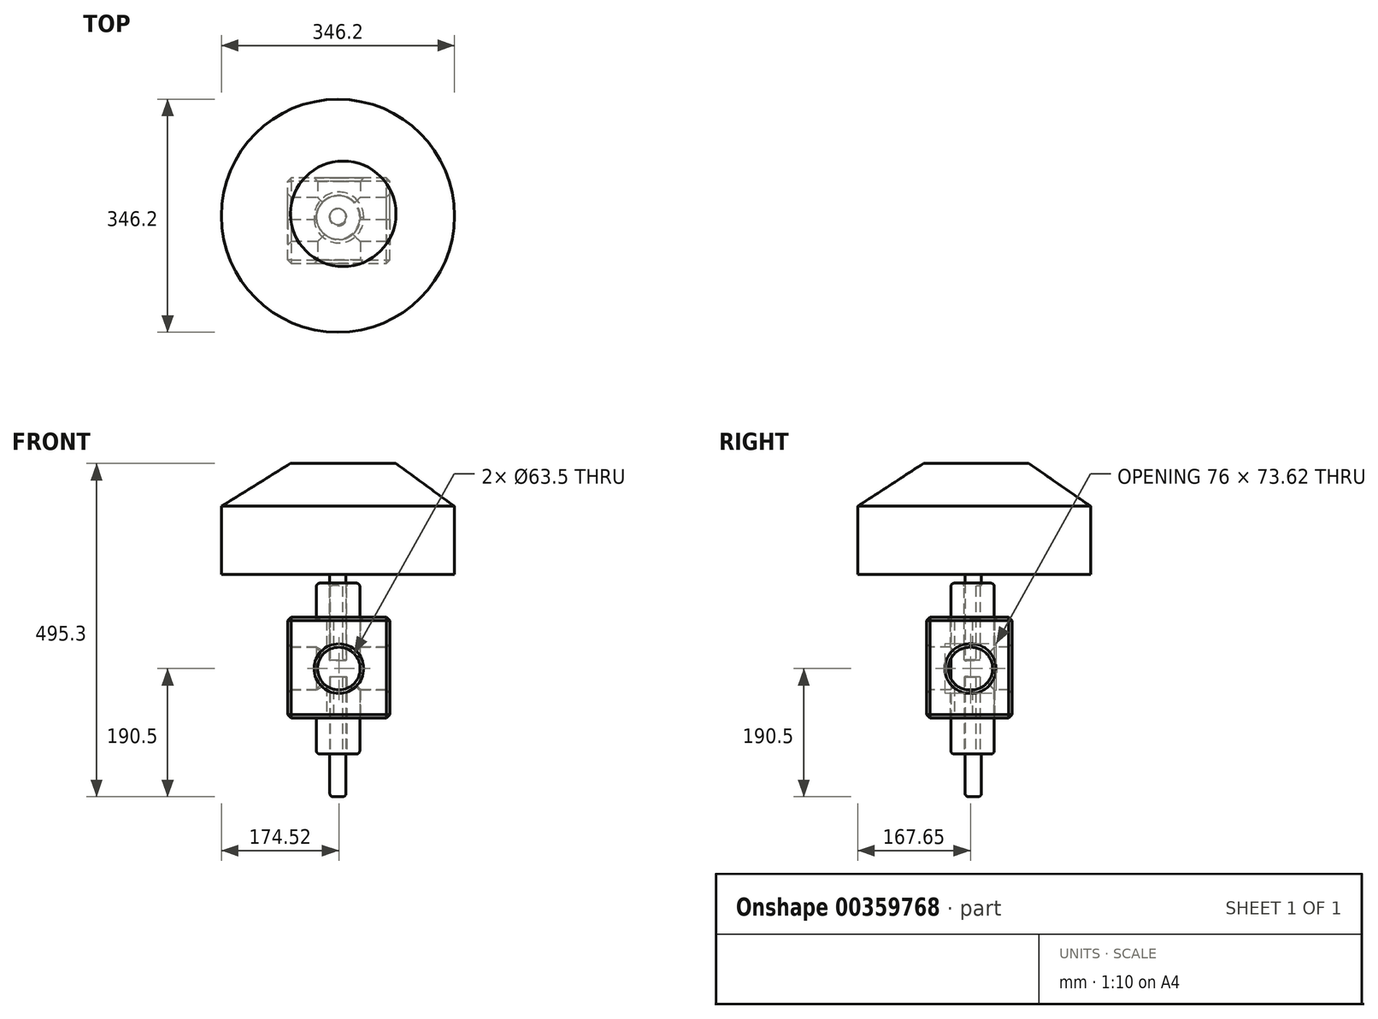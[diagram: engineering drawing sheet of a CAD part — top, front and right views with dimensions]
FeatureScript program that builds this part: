
annotation { "Feature Type Name" : "Feature", "Feature Type Description" : "" }
export const myFeature = defineFeature(function(context is Context, id is Id, definition is map)
    precondition{}
    {
        {
            var Q0;
            Q0=qCreatedBy(makeId("Front.planeOp"),FACE);
            var sketch = newSketch(context, id + "F0", { "sketchPlane" : qUnion([Q0])});
            skLineSegment(sketch, "E0.bottom", {"start": v(-76.3, 76.67) * mm, "end": v(75.69, 76.67) * mm});
            skLineSegment(sketch, "E0.top", {"start": v(-76.3, -73.65) * mm, "end": v(75.69, -73.65) * mm});
            skLineSegment(sketch, "E0.left", {"start": v(-76.3, 76.67) * mm, "end": v(-76.3, -73.65) * mm});
            skLineSegment(sketch, "E0.right", {"start": v(75.69, 76.67) * mm, "end": v(75.69, -73.65) * mm});
            skSolve(sketch);
        }
        {
            var Q0;
            Q0 = qSketchRegion(id + "F0", true);
            extrude(context, id + "F1", {"entities" : qUnion([Q0]), "depth" : 127 * mm});
        }
        {
            var Q0;
            Q0=makeQuery(id+"F1.opExtrude","CAP_FACE",FACE,{"disambiguationData":[OSD([sQuery(id+"F0.wireOp",EDGE,"E0.bottom"),sQuery(id+"F0.wireOp",EDGE,"E0.top"),sQuery(id+"F0.wireOp",EDGE,"E0.left"),sQuery(id+"F0.wireOp",EDGE,"E0.right")])],"isStart":false});
            var sketch = newSketch(context, id + "F2", { "sketchPlane" : qUnion([Q0])});
            skPoint(sketch, "E1", {"position": v(0, 0) * mm});
            skSolve(sketch);
        }
        {
            var Q0;
            Q0=makeQuery(id+"F1.opExtrude","CAP_FACE",FACE,{"disambiguationData":[OSD([sQuery(id+"F0.wireOp",EDGE,"E0.bottom"),sQuery(id+"F0.wireOp",EDGE,"E0.top"),sQuery(id+"F0.wireOp",EDGE,"E0.left"),sQuery(id+"F0.wireOp",EDGE,"E0.right")])],"isStart":true});
            var sketch = newSketch(context, id + "F3", { "sketchPlane" : qUnion([Q0])});
            skPoint(sketch, "E2", {"position": v(0, 0) * mm});
            skSolve(sketch);
        }
        {
            var Q0;
            Q0=sQuery(id+"F2.wireOp",VERTEX,"E1");
            var Q1;
            Q1=sQuery(id+"F3.wireOp",VERTEX,"E2");
            var Q2;
            Q2=makeQuery(id+"F1.opExtrude","SWEPT_BODY",BODY,{"disambiguationData":[OSD([sQuery(id+"F0.wireOp",EDGE,"E0.bottom"),sQuery(id+"F0.wireOp",EDGE,"E0.top"),sQuery(id+"F0.wireOp",EDGE,"E0.left"),sQuery(id+"F0.wireOp",EDGE,"E0.right")])]});
            hole(context, id + "F4", {"style" : HoleStyle.SIMPLE, "endStyle" : HoleEndStyle.THROUGH, "holeDiameter" : 63.5 * mm, "isTappedThrough" : true, "tappedDepth" : 12.7 * mm, "tapClearance" : 3, "locations" : qUnion([Q0, Q1]), "scope" : qUnion([Q2])});
        }
        {
            var Q0;
            Q0=makeQuery(id+"F1.opExtrude","SWEPT_FACE",FACE,{"disambiguationData":[OSD([sQuery(id+"F0.wireOp",EDGE,"E0.top")])]});
            var sketch = newSketch(context, id + "F5", { "sketchPlane" : qUnion([Q0])});
            skPoint(sketch, "E3", {"position": v(0, 58.1) * mm});
            skSolve(sketch);
        }
        {
            var Q0;
            Q0=makeQuery(id+"F1.opExtrude","SWEPT_FACE",FACE,{"disambiguationData":[OSD([sQuery(id+"F0.wireOp",EDGE,"E0.bottom")])]});
            var sketch = newSketch(context, id + "F6", { "sketchPlane" : qUnion([Q0])});
            skPoint(sketch, "E4", {"position": v(0, -60.18) * mm});
            skSolve(sketch);
        }
        {
            var Q0;
            Q0=sQuery(id+"F6.wireOp",VERTEX,"E4");
            var Q1;
            Q1=sQuery(id+"F5.wireOp",VERTEX,"E3");
            var Q2;
            Q2=makeQuery(id+"F1.opExtrude","SWEPT_BODY",BODY,{"disambiguationData":[OSD([sQuery(id+"F0.wireOp",EDGE,"E0.bottom"),sQuery(id+"F0.wireOp",EDGE,"E0.top"),sQuery(id+"F0.wireOp",EDGE,"E0.left"),sQuery(id+"F0.wireOp",EDGE,"E0.right")])]});
            hole(context, id + "F7", {"style" : HoleStyle.SIMPLE, "endStyle" : HoleEndStyle.THROUGH, "holeDiameter" : 63.5 * mm, "isTappedThrough" : true, "tappedDepth" : 12.7 * mm, "tapClearance" : 3, "locations" : qUnion([Q0, Q1]), "scope" : qUnion([Q2])});
        }
        {
            var Q0;
            Q0=makeQuery(id+"F1.opExtrude","SWEPT_FACE",FACE,{"disambiguationData":[OSD([sQuery(id+"F0.wireOp",EDGE,"E0.right")])]});
            var sketch = newSketch(context, id + "F8", { "sketchPlane" : qUnion([Q0])});
            skPoint(sketch, "E5", {"position": v(-60.81, 0) * mm});
            skSolve(sketch);
        }
        {
            var Q0;
            Q0=makeQuery(id+"F1.opExtrude","SWEPT_FACE",FACE,{"disambiguationData":[OSD([sQuery(id+"F0.wireOp",EDGE,"E0.left")])]});
            var sketch = newSketch(context, id + "F9", { "sketchPlane" : qUnion([Q0])});
            skPoint(sketch, "E6", {"position": v(63.15, 0) * mm});
            skSolve(sketch);
        }
        {
            var Q0;
            Q0=sQuery(id+"F9.wireOp",VERTEX,"E6");
            var Q1;
            Q1=sQuery(id+"F8.wireOp",VERTEX,"E5");
            var Q2;
            Q2=makeQuery(id+"F1.opExtrude","SWEPT_BODY",BODY,{"disambiguationData":[OSD([sQuery(id+"F0.wireOp",EDGE,"E0.bottom"),sQuery(id+"F0.wireOp",EDGE,"E0.top"),sQuery(id+"F0.wireOp",EDGE,"E0.left"),sQuery(id+"F0.wireOp",EDGE,"E0.right")])]});
            hole(context, id + "F10", {"style" : HoleStyle.SIMPLE, "endStyle" : HoleEndStyle.THROUGH, "holeDiameter" : 63.5 * mm, "isTappedThrough" : true, "tappedDepth" : 12.7 * mm, "tapClearance" : 3, "locations" : qUnion([Q0, Q1]), "scope" : qUnion([Q2])});
        }
        {
            var Q0;
            Q0=makeQuery(id+"F1.opExtrude","SWEPT_FACE",FACE,{"disambiguationData":[OSD([sQuery(id+"F0.wireOp",EDGE,"E0.right")])]});
            var Q1;
            Q1=makeQuery(id+"F1.opExtrude","CAP_FACE",FACE,{"disambiguationData":[OSD([sQuery(id+"F0.wireOp",EDGE,"E0.bottom"),sQuery(id+"F0.wireOp",EDGE,"E0.top"),sQuery(id+"F0.wireOp",EDGE,"E0.left"),sQuery(id+"F0.wireOp",EDGE,"E0.right")])],"isStart":false});
            var Q2;
            Q2=makeQuery(id+"F1.opExtrude","SWEPT_FACE",FACE,{"disambiguationData":[OSD([sQuery(id+"F0.wireOp",EDGE,"E0.bottom")])]});
            var Q3;
            Q3=makeQuery(id+"F1.opExtrude","SWEPT_FACE",FACE,{"disambiguationData":[OSD([sQuery(id+"F0.wireOp",EDGE,"E0.left")])]});
            var Q4;
            Q4=makeQuery(id+"F1.opExtrude","CAP_FACE",FACE,{"disambiguationData":[OSD([sQuery(id+"F0.wireOp",EDGE,"E0.bottom"),sQuery(id+"F0.wireOp",EDGE,"E0.top"),sQuery(id+"F0.wireOp",EDGE,"E0.left"),sQuery(id+"F0.wireOp",EDGE,"E0.right")])],"isStart":true});
            chamfer(context, id + "F11", {"entities" : qUnion([Q0, Q1, Q2, Q3, Q4]), "width" : 5.08 * mm, "tangentPropagation" : true});
        }
        {
            var Q0;
            Q0=qCreatedBy(makeId("Top.planeOp"),FACE);
            var sketch = newSketch(context, id + "F12", { "sketchPlane" : qUnion([Q0])});
            skCircle(sketch, "E7", {"center": v(-1.17, -58.85) * mm, "radius": 32.2 * mm});
            skSolve(sketch);
        }
        {
            var Q0;
            Q0 = qSketchRegion(id + "F12", true);
            extrude(context, id + "F13", {"entities" : qUnion([Q0]), "operationType" : NewBodyOperationType.ADD, "endBound" : BoundingType.SYMMETRIC, "depth" : 254 * mm});
        }
        {
            var Q0;
            Q0=makeQuery(id+"F13.opExtrude","CAP_FACE",FACE,{"disambiguationData":[OSD([sQuery(id+"F12.wireOp",EDGE,"E7")])],"isStart":true});
            var sketch = newSketch(context, id + "F14", { "sketchPlane" : qUnion([Q0])});
            skPoint(sketch, "E8", {"position": v(-1.17, 58.85) * mm});
            skSolve(sketch);
        }
        {
            var Q0;
            Q0=makeQuery(id+"F13.opExtrude","CAP_FACE",FACE,{"disambiguationData":[OSD([sQuery(id+"F12.wireOp",EDGE,"E7")])],"isStart":false});
            var sketch = newSketch(context, id + "F15", { "sketchPlane" : qUnion([Q0])});
            skPoint(sketch, "E9", {"position": v(-1.17, -58.85) * mm});
            skSolve(sketch);
        }
        {
            var Q0;
            Q0=sQuery(id+"F15.wireOp",VERTEX,"E9");
            var Q1;
            Q1=sQuery(id+"F14.wireOp",VERTEX,"E8");
            var Q2;
            Q2=makeQuery(id+"F1.opExtrude","SWEPT_BODY",BODY,{"disambiguationData":[OSD([sQuery(id+"F0.wireOp",EDGE,"E0.bottom"),sQuery(id+"F0.wireOp",EDGE,"E0.top"),sQuery(id+"F0.wireOp",EDGE,"E0.left"),sQuery(id+"F0.wireOp",EDGE,"E0.right")])]});
            hole(context, id + "F16", {"style" : HoleStyle.SIMPLE, "endStyle" : HoleEndStyle.BLIND, "holeDiameter" : 25.4 * mm, "holeDepth" : 114.3 * mm, "isTappedThrough" : true, "tappedDepth" : 12.7 * mm, "tapClearance" : 3, "locations" : qUnion([Q0, Q1]), "scope" : qUnion([Q2])});
        }
        {
            var Q0;
            Q0=makeQuery(id+"F13.opExtrude","CAP_EDGE",EDGE,{"disambiguationData":[OSD([sQuery(id+"F12.wireOp",EDGE,"E7")])],"isStart":true});
            var Q1;
            Q1=makeQuery(id+"F13.opExtrude","CAP_FACE",FACE,{"disambiguationData":[OSD([sQuery(id+"F12.wireOp",EDGE,"E7")])],"isStart":false});
            var Q2;
            Q2=makeQuery(id+"F16.hole-1.boolean.opBoolean","COPY",EDGE,{"derivedFrom":makeQuery(id+"F16.hole-1.opRevolve","SWEPT_EDGE",EDGE,{"disambiguationData":[OSD([sQuery(id+"F16.hole-1.sketch.wireOp",EDGE,"core_line_2"),sQuery(id+"F16.hole-1.sketch.wireOp",EDGE,"core_line_3")])]})});
            fillet(context, id + "F17", {"entities" : qUnion([Q0, Q1, Q2]), "radius" : 5.08 * mm, "tangentPropagation" : true, "allowEdgeOverflow" : false});
        }
        {
            var Q0;
            Q0=qCreatedBy(makeId("Top.planeOp"),FACE);
            var sketch = newSketch(context, id + "F18", { "sketchPlane" : qUnion([Q0])});
            skCircle(sketch, "E10", {"center": v(-1.51, -57.85) * mm, "radius": 12.06 * mm});
            skSolve(sketch);
        }
        {
            var Q0;
            Q0 = qSketchRegion(id + "F18", true);
            extrude(context, id + "F19", {"entities" : qUnion([Q0]), "operationType" : NewBodyOperationType.ADD, "endBound" : BoundingType.SYMMETRIC, "depth" : 381 * mm});
        }
        {
            var Q0;
            Q0=makeQuery(id+"F19.opExtrude","CAP_FACE",FACE,{"disambiguationData":[OSD([sQuery(id+"F18.wireOp",EDGE,"E10")])],"isStart":true});
            var Q1;
            Q1=makeQuery(id+"F19.opExtrude","CAP_FACE",FACE,{"disambiguationData":[OSD([sQuery(id+"F18.wireOp",EDGE,"E10")])],"isStart":false});
            fillet(context, id + "F20", {"entities" : qUnion([Q0, Q1]), "radius" : 5.08 * mm, "tangentPropagation" : true, "allowEdgeOverflow" : false});
        }
        {
            var Q0;
            Q0=qCreatedBy(makeId("Top.planeOp"),FACE);
            cPlane(context, id + "F21", {"entities" : qUnion([Q0]), "cplaneType" : CPlaneType.OFFSET, "offset" : 190.5 * mm, "width" : 152.4 * mm, "height" : 152.4 * mm});
        }
        {
            var Q0;
            Q0=qCreatedBy(id+"F21.planeOp",FACE);
            var sketch = newSketch(context, id + "F22", { "sketchPlane" : qUnion([Q0])});
            skCircle(sketch, "E11", {"center": v(-1.42, -56.53) * mm, "radius": 173.1 * mm});
            skSolve(sketch);
        }
        {
            var Q0;
            Q0 = qSketchRegion(id + "F22", true);
            extrude(context, id + "F23", {"entities" : qUnion([Q0]), "operationType" : NewBodyOperationType.ADD, "endBound" : BoundingType.SYMMETRIC, "depth" : 101.6 * mm});
        }
        {
            var Q0;
            Q0=qCreatedBy(makeId("Top.planeOp"),FACE);
            cPlane(context, id + "F24", {"entities" : qUnion([Q0]), "cplaneType" : CPlaneType.OFFSET, "offset" : 304.8 * mm, "width" : 152.4 * mm, "height" : 152.4 * mm});
        }
        {
            var Q0;
            Q0=makeQuery(id+"F23.opExtrude","CAP_FACE",FACE,{"disambiguationData":[OSD([sQuery(id+"F22.wireOp",EDGE,"E11")])],"isStart":false});
            var sketch = newSketch(context, id + "F25", { "sketchPlane" : qUnion([Q0])});
            skPoint(sketch, "E12", {"position": v(-1.42, -56.53) * mm});
            skSolve(sketch);
        }
        {
            var Q0;
            Q0=qCreatedBy(id+"F24.planeOp",FACE);
            var sketch = newSketch(context, id + "F26", { "sketchPlane" : qUnion([Q0])});
            skCircle(sketch, "E13", {"center": v(6.43, -53.54) * mm, "radius": 78.38 * mm});
            skSolve(sketch);
        }
        {
            var Q0;
            Q0 = qSketchRegion(id + "F26", true);
            var Q1;
            Q1=makeQuery(id+"F25.imprint","IMPRINT",FACE,{"disambiguationData":[TD([[makeQuery(id+"F25.imprint","IMPRINT",EDGE,{"derivedFrom":makeQuery(id+"F23.opExtrude","CAP_EDGE",EDGE,{"disambiguationData":[OSD([sQuery(id+"F22.wireOp",EDGE,"E11")])],"isStart":false})}),1.0]])]});
            var Q2;
            Q2=sQuery(id+"F26.wireOp",EDGE,"E13");
            var Q3;
            Q3=makeQuery(id+"F25.imprint","IMPRINT",FACE,{"disambiguationData":[TD([[makeQuery(id+"F25.imprint","IMPRINT",EDGE,{"derivedFrom":makeQuery(id+"F23.opExtrude","CAP_EDGE",EDGE,{"disambiguationData":[OSD([sQuery(id+"F22.wireOp",EDGE,"E11")])],"isStart":false})}),1.0]])]});
            loft(context, id + "F27", {"sheetProfilesArray" : [{ "sheetProfileEntities" : qUnion([Q0]) }, { "sheetProfileEntities" : qUnion([Q1]) }], "wireProfilesArray" : [{ "wireProfileEntities" : qUnion([Q2]) }, { "wireProfileEntities" : qUnion([Q3]) }]});
        }
    });
